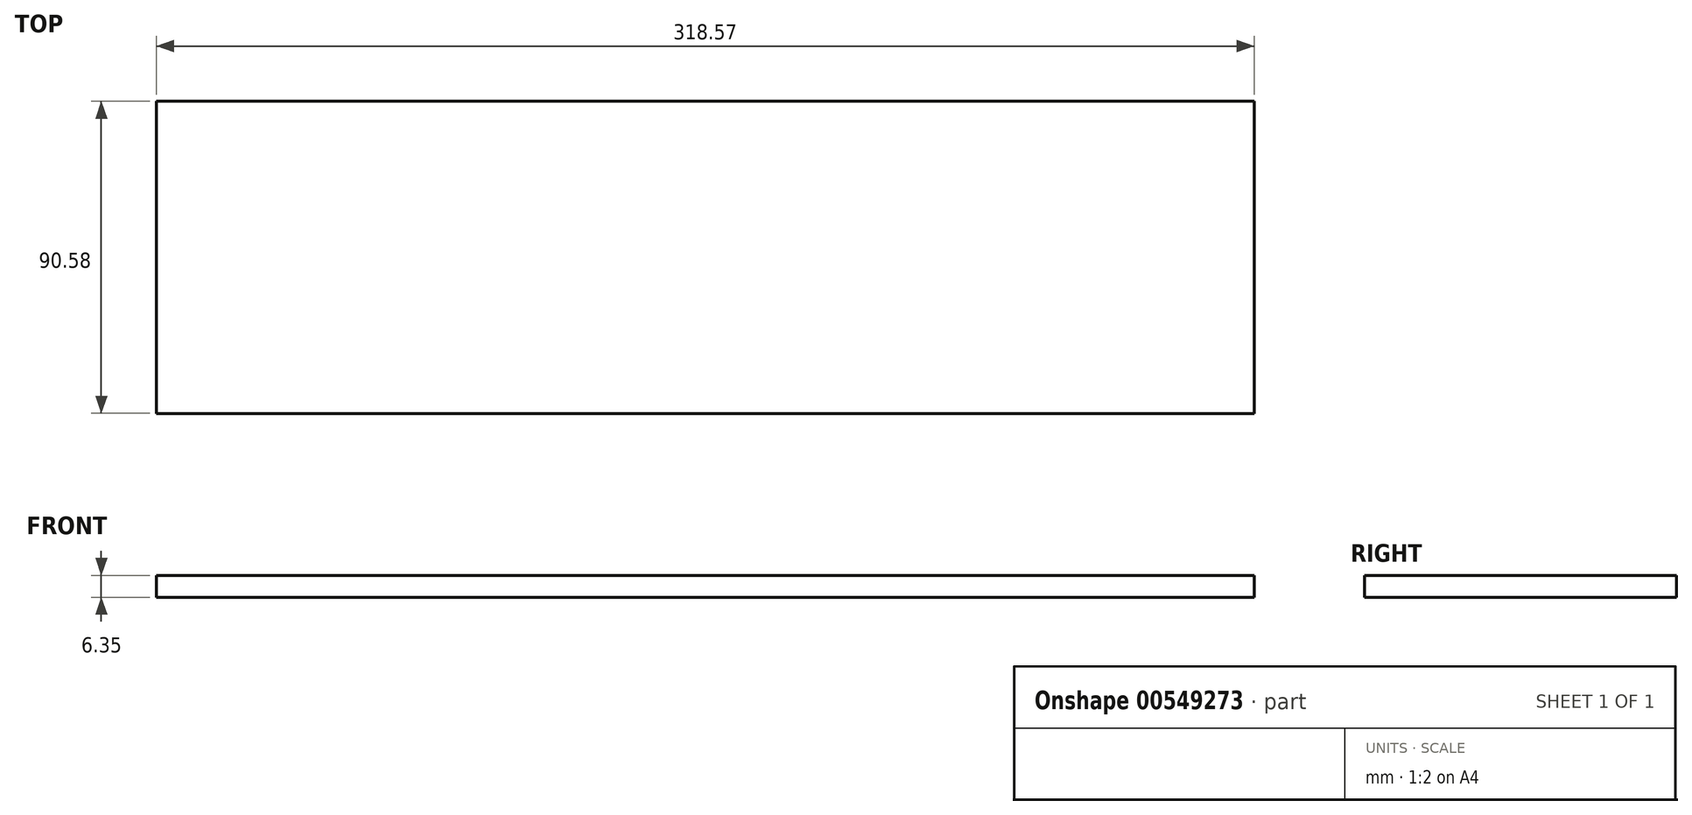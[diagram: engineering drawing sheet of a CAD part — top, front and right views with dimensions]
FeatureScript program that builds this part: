
annotation { "Feature Type Name" : "Feature", "Feature Type Description" : "" }
export const myFeature = defineFeature(function(context is Context, id is Id, definition is map)
    precondition{}
    {
        {
            var Q0;
            Q0=qCreatedBy(makeId("Top.planeOp"),FACE);
            var sketch = newSketch(context, id + "F0", { "sketchPlane" : qUnion([Q0])});
            skLineSegment(sketch, "E0.bottom", {"start": v(-981.06, 689.74) * mm, "end": v(-662.5, 689.74) * mm});
            skLineSegment(sketch, "E0.top", {"start": v(-981.06, 599.16) * mm, "end": v(-662.5, 599.16) * mm});
            skLineSegment(sketch, "E0.left", {"start": v(-981.06, 689.74) * mm, "end": v(-981.06, 599.16) * mm});
            skLineSegment(sketch, "E0.right", {"start": v(-662.5, 689.74) * mm, "end": v(-662.5, 599.16) * mm});
            skSolve(sketch);
        }
        {
            var Q0;
            Q0=makeQuery(id+"F0.imprint","IMPRINT",FACE,{"disambiguationData":[TD([[makeQuery(id+"F0.imprint","IMPRINT",EDGE,{"derivedFrom":sQuery(id+"F0.wireOp",EDGE,"E0.bottom")}),-1.0]])]});
            extrude(context, id + "F1", {"entities" : qUnion([Q0]), "depth" : 6.35 * mm, "offsetDistance" : 25.4 * mm});
        }
    });
